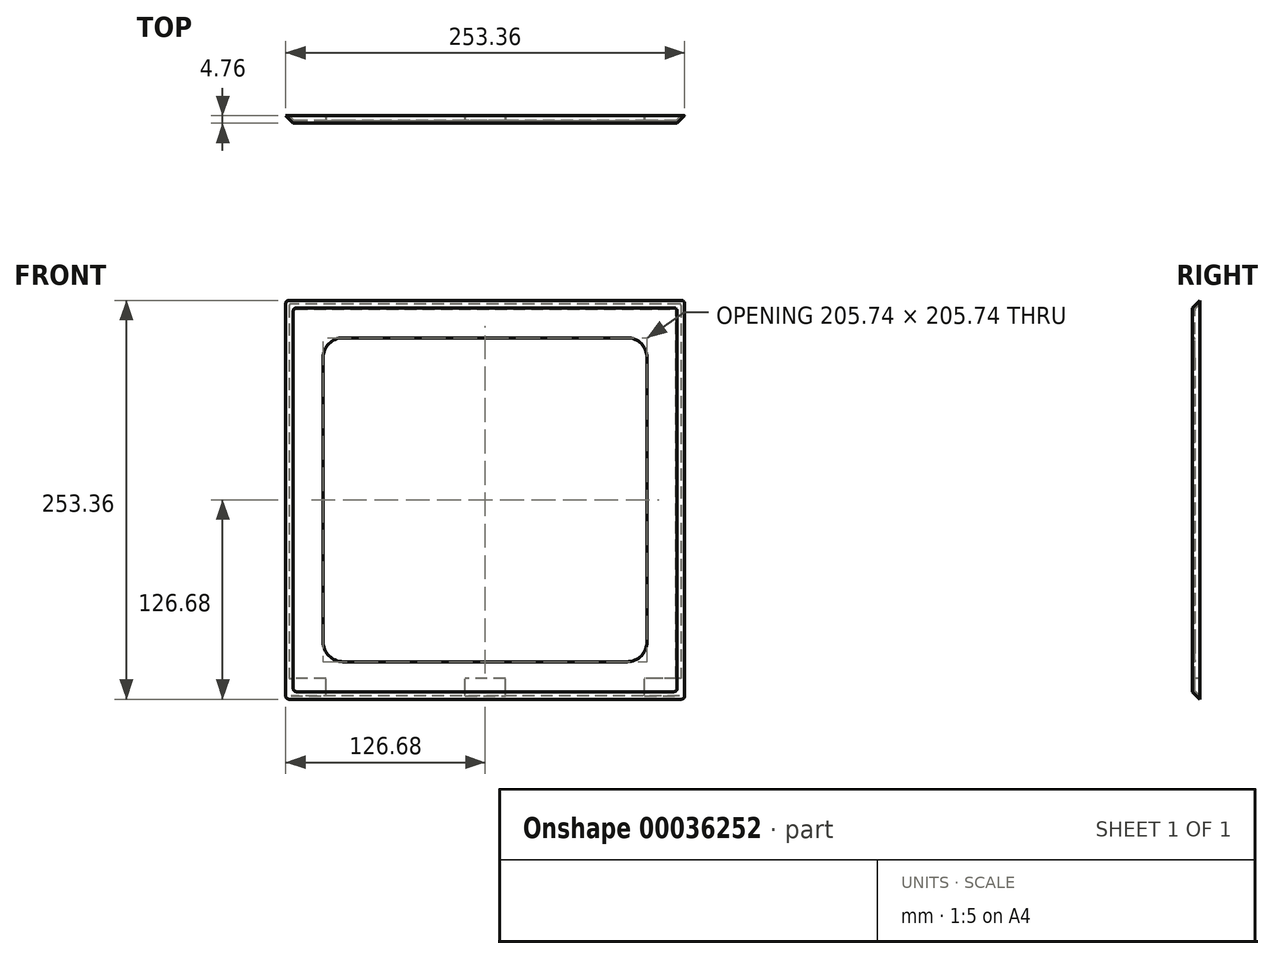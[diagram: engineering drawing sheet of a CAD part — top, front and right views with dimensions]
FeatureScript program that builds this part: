
annotation { "Feature Type Name" : "Feature", "Feature Type Description" : "" }
export const myFeature = defineFeature(function(context is Context, id is Id, definition is map)
    precondition{}
    {
        {
            var Q0;
            Q0=qCreatedBy(makeId("Front.planeOp"),FACE);
            var sketch = newSketch(context, id + "F0", { "sketchPlane" : qUnion([Q0])});
            skLineSegment(sketch, "E0.bottom", {"start": v(0, 0) * mm, "end": v(254, 0) * mm});
            skLineSegment(sketch, "E0.top", {"start": v(0, 254) * mm, "end": v(254, 254) * mm});
            skLineSegment(sketch, "E0.left", {"start": v(0, 0) * mm, "end": v(0, 254) * mm});
            skLineSegment(sketch, "E0.right", {"start": v(254, 0) * mm, "end": v(254, 254) * mm});
            skSolve(sketch);
        }
        {
            var Q0;
            Q0=qSketchRegion(id+"F0",true);
            extrude(context, id + "F1", {"entities" : qUnion([Q0]), "depth" : 4.76 * mm});
        }
        {
            var Q0;
            Q0=makeQuery(id+"F1.opExtrude","CAP_EDGE",EDGE,{"disambiguationData":[OSD([sQuery(id+"F0.wireOp",EDGE,"E0.left")])],"isStart":false});
            var Q1;
            Q1=makeQuery(id+"F1.opExtrude","CAP_EDGE",EDGE,{"disambiguationData":[OSD([sQuery(id+"F0.wireOp",EDGE,"E0.bottom")])],"isStart":false});
            var Q2;
            Q2=makeQuery(id+"F1.opExtrude","CAP_EDGE",EDGE,{"disambiguationData":[OSD([sQuery(id+"F0.wireOp",EDGE,"E0.right")])],"isStart":false});
            var Q3;
            Q3=makeQuery(id+"F1.opExtrude","CAP_EDGE",EDGE,{"disambiguationData":[OSD([sQuery(id+"F0.wireOp",EDGE,"E0.top")])],"isStart":false});
            chamfer(context, id + "F2", {"entities" : qUnion([Q0, Q1, Q2, Q3]), "width" : 5.08 * mm, "tangentPropagation" : true});
        }
        {
            var Q0;
            Q0=makeQuery(id+"F2.opChamfer","BLEND_EDGE",EDGE,{"blendedFrom":[makeQuery(id+"F1.opExtrude","CAP_EDGE",EDGE,{"disambiguationData":[OSD([sQuery(id+"F0.wireOp",EDGE,"E0.top")])],"isStart":false}),makeQuery(id+"F1.opExtrude","CAP_EDGE",EDGE,{"disambiguationData":[OSD([sQuery(id+"F0.wireOp",EDGE,"E0.right")])],"isStart":false})],"blendedInto":[]});
            var Q1;
            Q1=makeQuery(id+"F2.opChamfer","BLEND_EDGE",EDGE,{"blendedFrom":[makeQuery(id+"F1.opExtrude","CAP_EDGE",EDGE,{"disambiguationData":[OSD([sQuery(id+"F0.wireOp",EDGE,"E0.top")])],"isStart":false}),makeQuery(id+"F1.opExtrude","CAP_EDGE",EDGE,{"disambiguationData":[OSD([sQuery(id+"F0.wireOp",EDGE,"E0.left")])],"isStart":false})],"blendedInto":[]});
            var Q2;
            Q2=makeQuery(id+"F2.opChamfer","BLEND_EDGE",EDGE,{"blendedFrom":[makeQuery(id+"F1.opExtrude","CAP_EDGE",EDGE,{"disambiguationData":[OSD([sQuery(id+"F0.wireOp",EDGE,"E0.bottom")])],"isStart":false}),makeQuery(id+"F1.opExtrude","CAP_EDGE",EDGE,{"disambiguationData":[OSD([sQuery(id+"F0.wireOp",EDGE,"E0.right")])],"isStart":false})],"blendedInto":[]});
            var Q3;
            Q3=makeQuery(id+"F2.opChamfer","BLEND_EDGE",EDGE,{"blendedFrom":[makeQuery(id+"F1.opExtrude","CAP_EDGE",EDGE,{"disambiguationData":[OSD([sQuery(id+"F0.wireOp",EDGE,"E0.bottom")])],"isStart":false}),makeQuery(id+"F1.opExtrude","CAP_EDGE",EDGE,{"disambiguationData":[OSD([sQuery(id+"F0.wireOp",EDGE,"E0.left")])],"isStart":false})],"blendedInto":[]});
            fillet(context, id + "F3", {"entities" : qUnion([Q0, Q1, Q2, Q3]), "radius" : 3.17 * mm, "tangentPropagation" : true, "allowEdgeOverflow" : false});
        }
        {
            var Q0;
            Q0=makeQuery(id+"F1.opExtrude","CAP_FACE",FACE,{"disambiguationData":[OSD([sQuery(id+"F0.wireOp",EDGE,"E0.bottom"),sQuery(id+"F0.wireOp",EDGE,"E0.top"),sQuery(id+"F0.wireOp",EDGE,"E0.left"),sQuery(id+"F0.wireOp",EDGE,"E0.right")])],"isStart":true});
            shell(context, id + "F4", {"entities" : qUnion([Q0]), "thickness" : 1.59 * mm});
        }
        {
            var Q0;
            Q0=makeQuery(id+"F1.opExtrude","CAP_FACE",FACE,{"disambiguationData":[OSD([sQuery(id+"F0.wireOp",EDGE,"E0.bottom"),sQuery(id+"F0.wireOp",EDGE,"E0.top"),sQuery(id+"F0.wireOp",EDGE,"E0.left"),sQuery(id+"F0.wireOp",EDGE,"E0.right")])],"isStart":false});
            var sketch = newSketch(context, id + "F5", { "sketchPlane" : qUnion([Q0])});
            skLineSegment(sketch, "E1.0", {"start": v(24.13, 217.17) * mm, "end": v(24.13, 36.83) * mm});
            skLineSegment(sketch, "E1.1", {"start": v(217.17, 229.87) * mm, "end": v(36.83, 229.87) * mm});
            skLineSegment(sketch, "E1.2", {"start": v(229.87, 36.83) * mm, "end": v(229.87, 217.17) * mm});
            skLineSegment(sketch, "E1.3", {"start": v(36.83, 24.13) * mm, "end": v(217.17, 24.13) * mm});
            skPoint(sketch, "E2.visualSharp", {"position": v(24.13, 229.87) * mm});
            skArc(sketch, "E2.filletArc", {"start": v(36.83, 229.87) * mm, "mid": v(27.85, 226.15) * mm, "end": v(24.13, 217.17) * mm});
            skPoint(sketch, "E3.visualSharp", {"position": v(229.87, 229.87) * mm});
            skArc(sketch, "E3.filletArc", {"start": v(229.87, 217.17) * mm, "mid": v(226.15, 226.15) * mm, "end": v(217.17, 229.87) * mm});
            skPoint(sketch, "E4.visualSharp", {"position": v(24.13, 24.13) * mm});
            skArc(sketch, "E4.filletArc", {"start": v(24.13, 36.83) * mm, "mid": v(27.85, 27.85) * mm, "end": v(36.83, 24.13) * mm});
            skPoint(sketch, "E5.visualSharp", {"position": v(229.87, 24.13) * mm});
            skArc(sketch, "E5.filletArc", {"start": v(217.17, 24.13) * mm, "mid": v(226.15, 27.85) * mm, "end": v(229.87, 36.83) * mm});
            skSolve(sketch);
        }
        {
            var Q0;
            Q0=qSketchRegion(id+"F5",true);
            extrude(context, id + "F6", {"entities" : qUnion([Q0]), "operationType" : NewBodyOperationType.REMOVE, "oppositeDirection" : true, "depth" : 25.4 * mm});
        }
        {
            var Q0;
            Q0=makeQuery(id+"F1.opExtrude","CAP_FACE",FACE,{"disambiguationData":[OSD([sQuery(id+"F0.wireOp",EDGE,"E0.bottom"),sQuery(id+"F0.wireOp",EDGE,"E0.top"),sQuery(id+"F0.wireOp",EDGE,"E0.left"),sQuery(id+"F0.wireOp",EDGE,"E0.right")])],"isStart":true});
            var sketch = newSketch(context, id + "F7", { "sketchPlane" : qUnion([Q0])});
            skLineSegment(sketch, "E6.top", {"start": v(-253.68, 13.68) * mm, "end": v(-228.28, 13.68) * mm});
            skLineSegment(sketch, "E6.left", {"start": v(-253.68, 2.56) * mm, "end": v(-253.68, 13.68) * mm});
            skLineSegment(sketch, "E6.right", {"start": v(-228.28, 2.56) * mm, "end": v(-228.28, 13.68) * mm});
            skLineSegment(sketch, "E7", {"start": v(-228.28, 2.56) * mm, "end": v(-253.68, 2.56) * mm});
            skPoint(sketch, "E8.orphan", {"position": v(-253.68, 0) * mm});
            skLineSegment(sketch, "E9.1.0.0", {"start": v(-139.76, 13.68) * mm, "end": v(-114.36, 13.68) * mm});
            skLineSegment(sketch, "E9.1.0.1", {"start": v(-114.36, 2.56) * mm, "end": v(-114.36, 13.68) * mm});
            skLineSegment(sketch, "E9.1.0.2", {"start": v(-114.36, 2.56) * mm, "end": v(-139.76, 2.56) * mm});
            skLineSegment(sketch, "E9.1.0.3", {"start": v(-139.76, 2.56) * mm, "end": v(-139.76, 13.68) * mm});
            skLineSegment(sketch, "E9.2.0.0", {"start": v(-25.84, 13.68) * mm, "end": v(-0.44, 13.68) * mm});
            skLineSegment(sketch, "E9.2.0.1", {"start": v(-0.44, 2.56) * mm, "end": v(-0.44, 13.68) * mm});
            skLineSegment(sketch, "E9.2.0.2", {"start": v(-0.44, 2.56) * mm, "end": v(-25.84, 2.56) * mm});
            skLineSegment(sketch, "E9.2.0.3", {"start": v(-25.84, 2.56) * mm, "end": v(-25.84, 13.68) * mm});
            skLineSegment(sketch, "E9.direction1", {"start": v(-253.68, 13.68) * mm, "end": v(-139.76, 13.68) * mm, "construction": true});
            skSolve(sketch);
        }
        {
            var Q0;
            {var subQ13=sQuery(id+"F7.wireOp",EDGE,"E6.right");Q0=makeQuery(id+"F7.imprint","IMPRINT",FACE,{"disambiguationData":[TD([[makeQuery(id+"F7.imprint","IMPRINT",EDGE,{"derivedFrom":subQ13}),1.0]])]});}
            var Q1;
            Q1=makeQuery(id+"F7.imprint","IMPRINT",FACE,{"disambiguationData":[TD([[makeQuery(id+"F7.imprint","IMPRINT",EDGE,{"derivedFrom":sQuery(id+"F7.wireOp",EDGE,"E9.1.0.0")}),-1.0]])]});
            var Q2;
            {var subQ13=sQuery(id+"F7.wireOp",EDGE,"E9.2.0.3");Q2=makeQuery(id+"F7.imprint","IMPRINT",FACE,{"disambiguationData":[TD([[makeQuery(id+"F7.imprint","IMPRINT",EDGE,{"derivedFrom":subQ13}),-1.0]])]});}
            extrude(context, id + "F8", {"entities" : qUnion([Q0, Q1, Q2]), "operationType" : NewBodyOperationType.ADD, "endBound" : BoundingType.UP_TO_NEXT, "oppositeDirection" : true, "depth" : 25.4 * mm});
        }
    });
